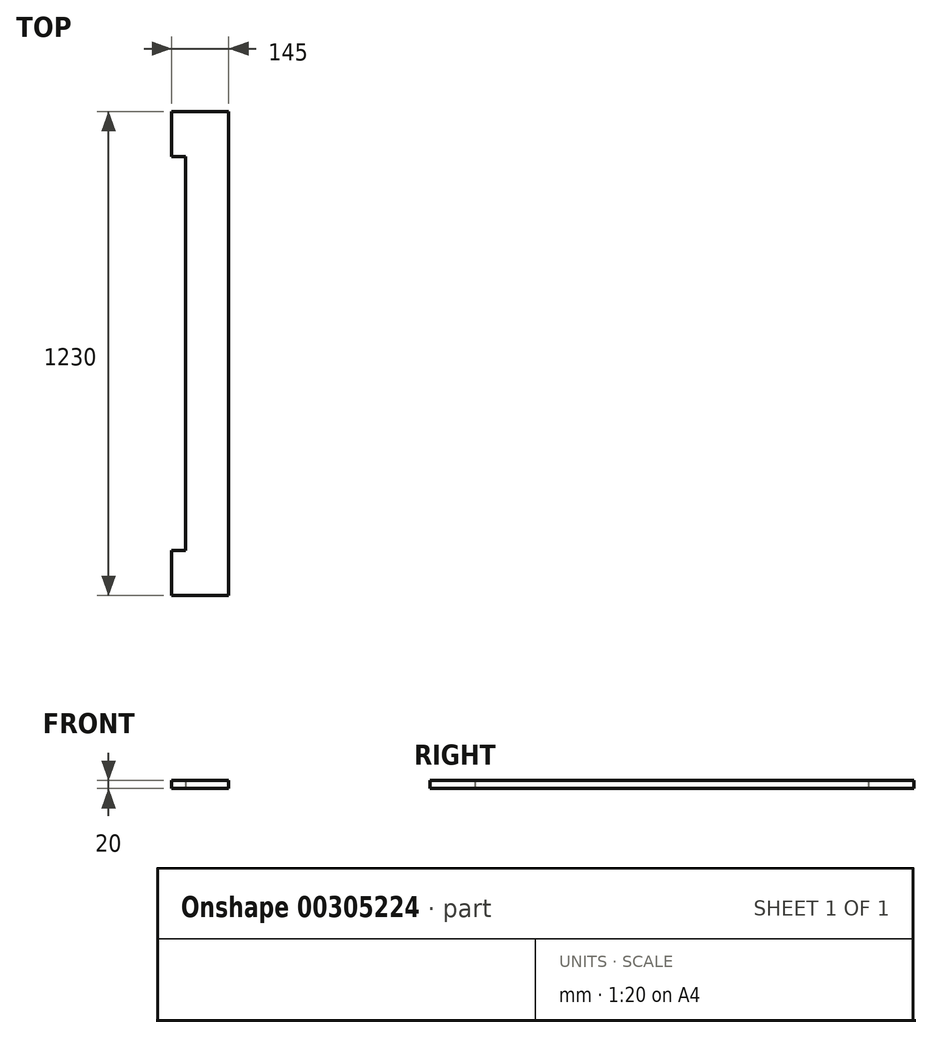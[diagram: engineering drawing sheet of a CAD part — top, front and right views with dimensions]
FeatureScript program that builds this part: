
annotation { "Feature Type Name" : "Feature", "Feature Type Description" : "" }
export const myFeature = defineFeature(function(context is Context, id is Id, definition is map)
    precondition{}
    {
        {
            var Q0;
            Q0=qCreatedBy(makeId("Front.planeOp"),FACE);
            var sketch = newSketch(context, id + "F0", { "sketchPlane" : qUnion([Q0])});
            skLineSegment(sketch, "E0.bottom", {"start": v(0, 0) * mm, "end": v(120, 0) * mm});
            skLineSegment(sketch, "E0.top", {"start": v(0, 20) * mm, "end": v(120, 20) * mm});
            skLineSegment(sketch, "E0.left", {"start": v(0, 0) * mm, "end": v(0, 20) * mm});
            skLineSegment(sketch, "E0.right", {"start": v(120, 0) * mm, "end": v(120, 20) * mm});
            skSolve(sketch);
        }
        {
            var Q0;
            Q0=makeQuery(id+"F0.imprint","IMPRINT",FACE,{"disambiguationData":[TD([[makeQuery(id+"F0.imprint","IMPRINT",EDGE,{"derivedFrom":sQuery(id+"F0.wireOp",EDGE,"E0.bottom")}),1.0]])]});
            extrude(context, id + "F1", {"entities" : qUnion([Q0]), "depth" : 1200 * mm});
        }
        {
            var Q0;
            Q0=makeQuery(id+"F1.opExtrude","CAP_FACE",FACE,{"disambiguationData":[OSD([sQuery(id+"F0.wireOp",EDGE,"E0.bottom"),sQuery(id+"F0.wireOp",EDGE,"E0.top"),sQuery(id+"F0.wireOp",EDGE,"E0.left"),sQuery(id+"F0.wireOp",EDGE,"E0.right")])],"isStart":false});
            extrude(context, id + "F2", {"entities" : qUnion([Q0]), "operationType" : NewBodyOperationType.ADD, "depth" : 15 * mm});
        }
        {
            var Q0;
            Q0=makeQuery(id+"F1.opExtrude","CAP_FACE",FACE,{"disambiguationData":[OSD([sQuery(id+"F0.wireOp",EDGE,"E0.bottom"),sQuery(id+"F0.wireOp",EDGE,"E0.top"),sQuery(id+"F0.wireOp",EDGE,"E0.left"),sQuery(id+"F0.wireOp",EDGE,"E0.right")])],"isStart":true});
            extrude(context, id + "F3", {"entities" : qUnion([Q0]), "operationType" : NewBodyOperationType.ADD, "depth" : 15 * mm});
        }
        {
            var Q0;
            {var subQ0=sQuery(id+"F0.wireOp",EDGE,"E0.left");Q0=makeQuery(id+"F3.boolean.opBoolean","MERGE",FACE,{"derivedFrom":[makeQuery(id+"F2.boolean.opBoolean","MERGE",FACE,{"derivedFrom":[makeQuery(id+"F1.opExtrude","SWEPT_FACE",FACE,{"disambiguationData":[OSD([subQ0])]}),makeQuery(id+"F2.opExtrude","SWEPT_FACE",FACE,{"disambiguationData":[OSD([subQ0])]})]}),makeQuery(id+"F3.opExtrude","SWEPT_FACE",FACE,{"disambiguationData":[OSD([subQ0])]})]});}
            var sketch = newSketch(context, id + "F4", { "sketchPlane" : qUnion([Q0])});
            skLineSegment(sketch, "E1.bottom", {"start": v(-15, 20) * mm, "end": v(100, 20) * mm});
            skLineSegment(sketch, "E1.top", {"start": v(-15, 0) * mm, "end": v(100, 0) * mm});
            skLineSegment(sketch, "E1.left", {"start": v(-15, 20) * mm, "end": v(-15, 0) * mm});
            skLineSegment(sketch, "E1.right", {"start": v(100, 20) * mm, "end": v(100, 0) * mm});
            skLineSegment(sketch, "E2.bottom", {"start": v(1215, 20) * mm, "end": v(1100, 20) * mm});
            skLineSegment(sketch, "E2.top", {"start": v(1215, 0) * mm, "end": v(1100, 0) * mm});
            skLineSegment(sketch, "E2.left", {"start": v(1215, 20) * mm, "end": v(1215, 0) * mm});
            skLineSegment(sketch, "E2.right", {"start": v(1100, 20) * mm, "end": v(1100, 0) * mm});
            skSolve(sketch);
        }
        {
            var Q0;
            Q0=makeQuery(id+"F4.imprint","IMPRINT",FACE,{"disambiguationData":[TD([[makeQuery(id+"F4.imprint","IMPRINT",EDGE,{"derivedFrom":sQuery(id+"F4.wireOp",EDGE,"E2.bottom")}),1.0]])]});
            extrude(context, id + "F5", {"entities" : qUnion([Q0]), "operationType" : NewBodyOperationType.ADD, "depth" : 25 * mm});
        }
        {
            var Q0;
            Q0=makeQuery(id+"F4.imprint","IMPRINT",FACE,{"disambiguationData":[TD([[makeQuery(id+"F4.imprint","IMPRINT",EDGE,{"derivedFrom":sQuery(id+"F4.wireOp",EDGE,"E1.bottom")}),1.0]])]});
            extrude(context, id + "F6", {"entities" : qUnion([Q0]), "operationType" : NewBodyOperationType.ADD, "depth" : 25 * mm});
        }
        {
            var Q0;
            {var subQ0=sQuery(id+"F4.wireOp",EDGE,"E1.right");Q0=makeQuery(id+"F4.imprint","IMPRINT",FACE,{"disambiguationData":[TD([[makeQuery(id+"F4.imprint","IMPRINT",EDGE,{"derivedFrom":subQ0}),1.0]])]});}
            var sketch = newSketch(context, id + "F7", { "sketchPlane" : qUnion([Q0])});
            skLineSegment(sketch, "E3.0.0", {"start": v(1100, 0) * mm, "end": v(1100, 20) * mm});
            skLineSegment(sketch, "E3.0.1", {"start": v(1100, 20) * mm, "end": v(100, 20) * mm});
            skLineSegment(sketch, "E3.0.2", {"start": v(100, 20) * mm, "end": v(100, 0) * mm});
            skLineSegment(sketch, "E3.0.3", {"start": v(100, 0) * mm, "end": v(1100, 0) * mm});
            skSolve(sketch);
        }
        {
            var Q0;
            Q0=makeQuery(id+"F7.imprint","IMPRINT",FACE,{"disambiguationData":[TD([[makeQuery(id+"F7.imprint","IMPRINT",EDGE,{"derivedFrom":sQuery(id+"F7.wireOp",EDGE,"E3.0.0")}),-1.0]])]});
            extrude(context, id + "F8", {"entities" : qUnion([Q0]), "operationType" : NewBodyOperationType.REMOVE, "oppositeDirection" : true, "depth" : 10 * mm});
        }
    });
